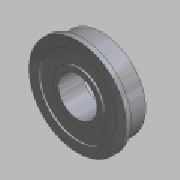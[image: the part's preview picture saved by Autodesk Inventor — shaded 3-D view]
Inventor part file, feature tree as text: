
AUTODESK INVENTOR PART (.ipt)
format: ipt  version: 2012 (Build 160160000, 160)  size: 107,008 bytes
history: native  units: mm (DEFAULTED — no unit token found)
features: extrude x4, sketch x4, plane x1
ambient origin geometry x8: Origin, YZ Plane, XZ Plane, XY Plane, X Axis, Y Axis, Z Axis, Center Point
bodies: Solid1 (feature_tree)
feature tree (9):
  extrude  "Extrusion1"  Depth=12.7mm
  plane  "Work Plane1"
  extrude  "Extrusion2"  Depth=7.9375mm TaperAngle=0.0deg
  extrude  "Extrusion3"  Depth=16.256mm
  extrude  "Extrusion4"  Depth=25.4mm
  sketch  "Sketch1"  dims[d9=1.424097mm d32=12.7mm]
  sketch  "Sketch2"  dims[d33=16.256mm d35=7.9375mm d36=0.0mm]
  sketch  "Sketch3"  dims[d37=25.4mm d38=16.256mm]
  sketch  "Sketch4"  dims[d39=6.6675mm d40=0.0mm d41=25.4mm d42=28.575mm d43=7.9375mm d44=0.0mm d45=31.75mm d46=28.575mm d47=1.5875mm d48=0.0mm]
